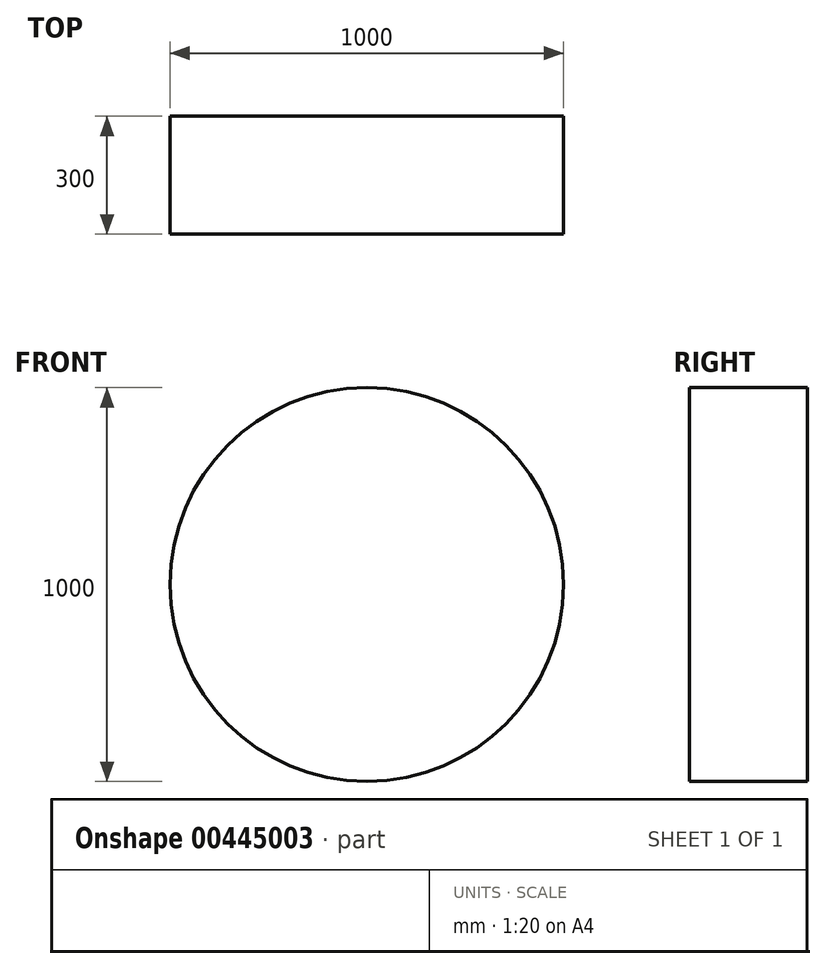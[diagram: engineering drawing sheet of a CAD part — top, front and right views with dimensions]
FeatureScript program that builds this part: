
annotation { "Feature Type Name" : "Feature", "Feature Type Description" : "" }
export const myFeature = defineFeature(function(context is Context, id is Id, definition is map)
    precondition{}
    {
        {
            var Q0;
            Q0=qCreatedBy(makeId("Front.planeOp"),FACE);
            var sketch = newSketch(context, id + "F0", { "sketchPlane" : qUnion([Q0])});
            skCircle(sketch, "E0", {"center": v(0, 0) * mm, "radius": 500 * mm});
            skSolve(sketch);
        }
        {
            var Q0;
            Q0=makeQuery(id+"F0.imprint","IMPRINT",FACE,{"disambiguationData":[TD([[makeQuery(id+"F0.imprint","IMPRINT",EDGE,{"derivedFrom":sQuery(id+"F0.wireOp",EDGE,"E0")}),1.0]])]});
            extrude(context, id + "F1", {"entities" : qUnion([Q0]), "depth" : 300 * mm});
        }
    });
